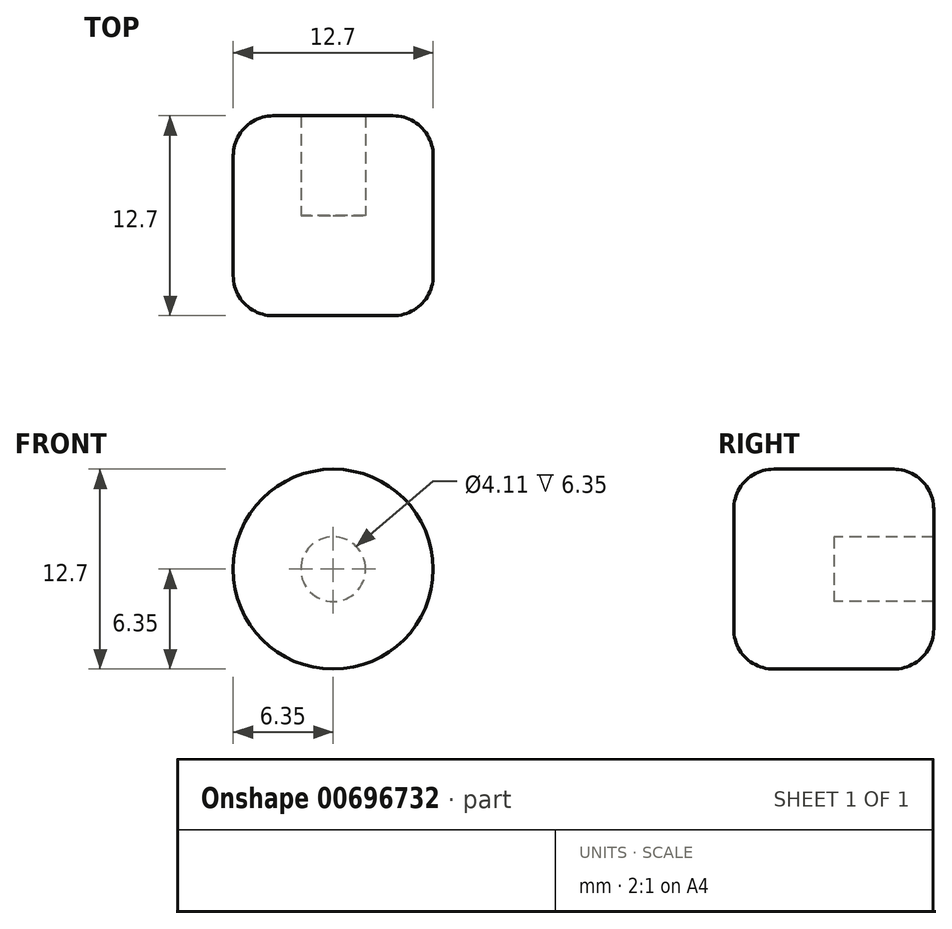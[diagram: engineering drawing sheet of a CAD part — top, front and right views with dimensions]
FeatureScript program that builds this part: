
annotation { "Feature Type Name" : "Feature", "Feature Type Description" : "" }
export const myFeature = defineFeature(function(context is Context, id is Id, definition is map)
    precondition{}
    {
        {
            var Q0;
            Q0=qCreatedBy(makeId("Front.planeOp"),FACE);
            var sketch = newSketch(context, id + "F0", { "sketchPlane" : qUnion([Q0])});
            skCircle(sketch, "E0", {"center": v(0, 0) * mm, "radius": 6.35 * mm});
            skSolve(sketch);
        }
        {
            var Q0;
            Q0=makeQuery(id+"F0.imprint","IMPRINT",FACE,{"disambiguationData":[TD([[makeQuery(id+"F0.imprint","IMPRINT",EDGE,{"derivedFrom":sQuery(id+"F0.wireOp",EDGE,"E0")}),1.0]])]});
            extrude(context, id + "F1", {"entities" : qUnion([Q0]), "depth" : 6.35 * mm, "offsetDistance" : 25.4 * mm});
        }
        {
            var Q0;
            Q0=makeQuery(id+"F1.opExtrude","CAP_FACE",FACE,{"disambiguationData":[OSD([sQuery(id+"F0.wireOp",EDGE,"E0")])],"isStart":true});
            var sketch = newSketch(context, id + "F2", { "sketchPlane" : qUnion([Q0])});
            skCircle(sketch, "E1", {"center": v(0, 0) * mm, "radius": 6.35 * mm});
            skCircle(sketch, "E2", {"center": v(0, 0) * mm, "radius": 2.06 * mm});
            skSolve(sketch);
        }
        {
            var Q0;
            Q0=qSketchRegion(id+"F2",true);
            extrude(context, id + "F3", {"entities" : qUnion([Q0]), "operationType" : NewBodyOperationType.ADD, "depth" : 6.35 * mm, "offsetDistance" : 25.4 * mm});
        }
        {
            var Q0;
            Q0=makeQuery(id+"F1.opExtrude","CAP_EDGE",EDGE,{"disambiguationData":[OSD([sQuery(id+"F0.wireOp",EDGE,"E0")])],"isStart":false});
            var Q1;
            Q1=makeQuery(id+"F3.opExtrude","CAP_EDGE",EDGE,{"disambiguationData":[OSD([sQuery(id+"F2.wireOp",EDGE,"E1")])],"isStart":false});
            fillet(context, id + "F4", {"entities" : qUnion([Q0, Q1]), "radius" : 2.54 * mm, "tangentPropagation" : true, "allowEdgeOverflow" : false});
        }
    });
